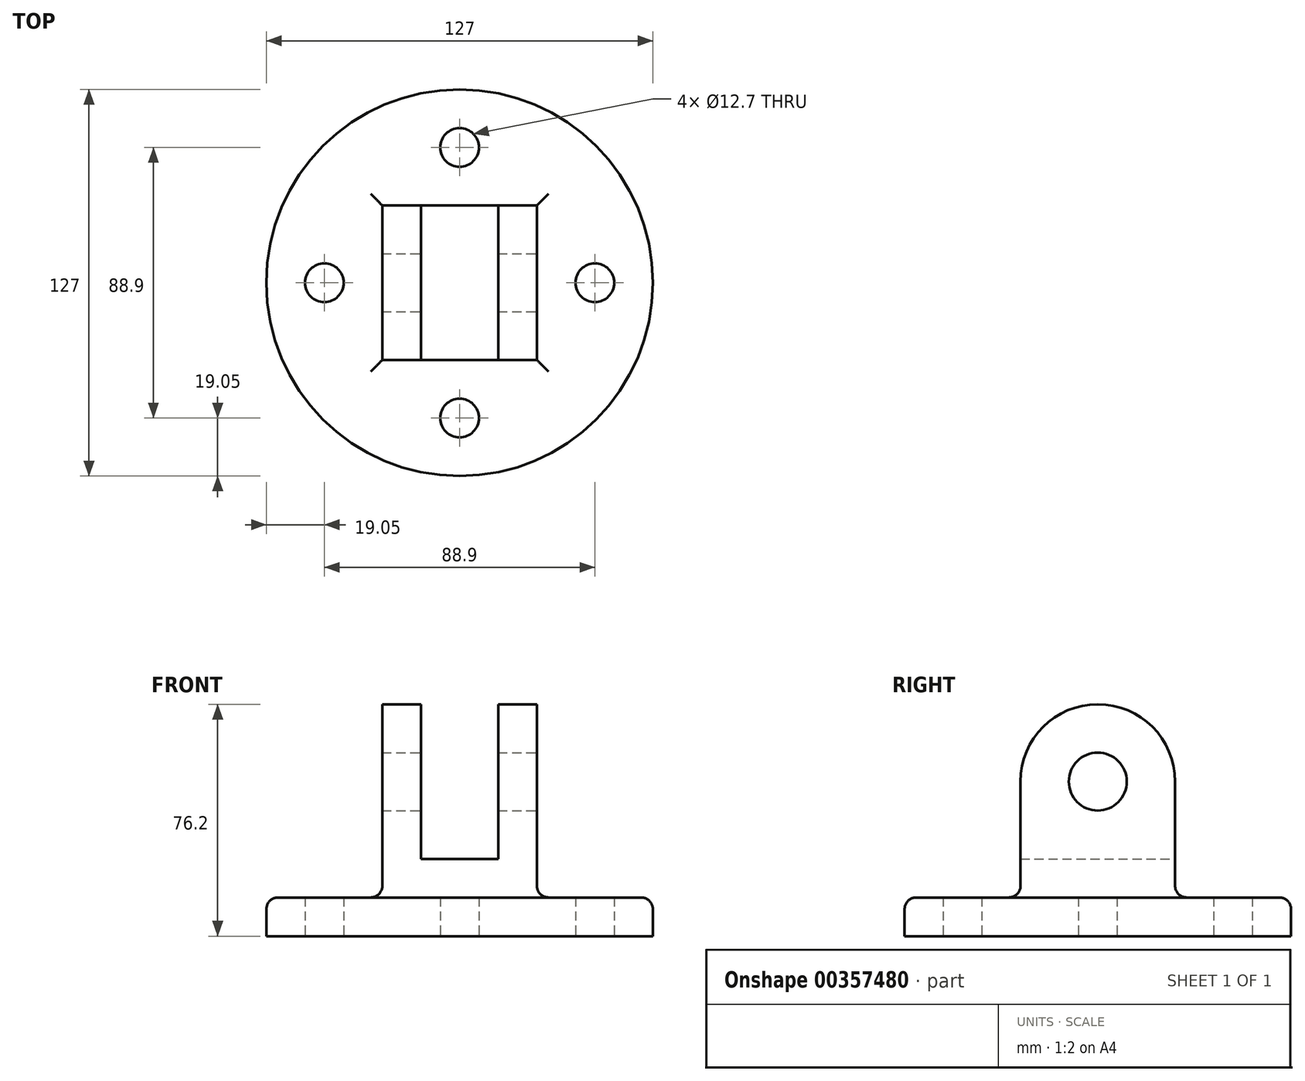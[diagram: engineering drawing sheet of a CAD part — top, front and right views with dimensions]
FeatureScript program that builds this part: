
annotation { "Feature Type Name" : "Feature", "Feature Type Description" : "" }
export const myFeature = defineFeature(function(context is Context, id is Id, definition is map)
    precondition{}
    {
        {
            var Q0;
            Q0=qCreatedBy(makeId("Top.planeOp"),FACE);
            var sketch = newSketch(context, id + "F0", { "sketchPlane" : qUnion([Q0])});
            skCircle(sketch, "E0", {"center": v(0, 0) * mm, "radius": 63.5 * mm});
            skCircle(sketch, "E1", {"center": v(0, 0) * mm, "radius": 44.45 * mm, "construction": true});
            skCircle(sketch, "E2", {"center": v(0, 44.45) * mm, "radius": 6.35 * mm});
            skCircle(sketch, "E3", {"center": v(-44.45, 0) * mm, "radius": 6.35 * mm});
            skCircle(sketch, "E4", {"center": v(44.45, 0) * mm, "radius": 6.35 * mm});
            skCircle(sketch, "E5", {"center": v(0, -44.45) * mm, "radius": 6.35 * mm});
            skSolve(sketch);
        }
        {
            var Q0;
            Q0 = qSketchRegion(id + "F0", true);
            extrude(context, id + "F1", {"entities" : qUnion([Q0]), "depth" : 12.7 * mm});
        }
        {
            var Q0;
            Q0=qCreatedBy(makeId("Front.planeOp"),FACE);
            var sketch = newSketch(context, id + "F2", { "sketchPlane" : qUnion([Q0])});
            skLineSegment(sketch, "E6", {"start": v(-25.4, 0) * mm, "end": v(25.4, 0) * mm});
            skLineSegment(sketch, "E7", {"start": v(-25.4, 0) * mm, "end": v(-25.4, 76.2) * mm});
            skLineSegment(sketch, "E8", {"start": v(25.4, 76.2) * mm, "end": v(25.4, 0) * mm});
            skLineSegment(sketch, "E9", {"start": v(-25.4, 76.2) * mm, "end": v(-12.7, 76.2) * mm});
            skLineSegment(sketch, "E10", {"start": v(-12.7, 76.2) * mm, "end": v(-12.7, 25.4) * mm});
            skLineSegment(sketch, "E11", {"start": v(-12.7, 25.4) * mm, "end": v(12.7, 25.4) * mm});
            skLineSegment(sketch, "E12", {"start": v(12.7, 25.4) * mm, "end": v(12.7, 76.2) * mm});
            skLineSegment(sketch, "E13", {"start": v(12.7, 76.2) * mm, "end": v(25.4, 76.2) * mm});
            skLineSegment(sketch, "E14", {"start": v(0, 70.93) * mm, "end": v(0, -31.27) * mm});
            skSolve(sketch);
        }
        {
            var Q0;
            Q0 = qSketchRegion(id + "F2", true);
            extrude(context, id + "F3", {"entities" : qUnion([Q0]), "operationType" : NewBodyOperationType.ADD, "depth" : 25.4 * mm, "hasSecondDirection" : true, "secondDirectionOppositeDirection" : true, "secondDirectionDepth" : 25.4 * mm});
        }
        {
            var Q0;
            Q0=makeQuery(id+"F3.opExtrude","SWEPT_FACE",FACE,{"disambiguationData":[OSD([sQuery(id+"F2.wireOp",EDGE,"E8")])]});
            var sketch = newSketch(context, id + "F4", { "sketchPlane" : qUnion([Q0])});
            skLineSegment(sketch, "E15", {"start": v(-25.4, 12.7) * mm, "end": v(25.4, 12.7) * mm});
            skLineSegment(sketch, "E16", {"start": v(-25.4, 12.7) * mm, "end": v(-25.4, 50.8) * mm});
            skLineSegment(sketch, "E17", {"start": v(25.4, 12.7) * mm, "end": v(25.4, 50.8) * mm});
            skArc(sketch, "E18", {"start": v(25.4, 50.8) * mm, "mid": v(0, 76.2) * mm, "end": v(-25.4, 50.8) * mm});
            skCircle(sketch, "E19", {"center": v(0, 50.8) * mm, "radius": 9.53 * mm});
            skSolve(sketch);
        }
        {
            var Q0;
            Q0=makeQuery(id+"F4.imprint","IMPRINT",FACE,{"disambiguationData":[TD([[makeQuery(id+"F4.imprint","IMPRINT",EDGE,{"derivedFrom":sQuery(id+"F4.wireOp",EDGE,"E19")}),1.0]])]});
            var Q1;
            {var subQ0=sQuery(id+"F4.wireOp",EDGE,"E18");var subQ1=sQuery(id+"F2.wireOp",EDGE,"E8");var subQ2=makeQuery(id+"F3.opExtrude","CAP_EDGE",EDGE,{"disambiguationData":[OSD([subQ1])],"isStart":true});var subQ3=makeQuery(id+"F4.imprint","INTERSECT",VERTEX,{"derivedFrom":[subQ2,sQuery(id+"F4.wireOp",EDGE,"E17"),subQ0]});Q1=makeQuery(id+"F4.imprint","IMPRINT",FACE,{"disambiguationData":[TD([[makeQuery(id+"F4.imprint","IMPRINT",EDGE,{"disambiguationData":[TD([[subQ3,-1.0]])],"derivedFrom":subQ0}),-1.0]])]});}
            var Q2;
            {var subQ0=sQuery(id+"F4.wireOp",EDGE,"E18");var subQ1=sQuery(id+"F2.wireOp",EDGE,"E8");var subQ2=makeQuery(id+"F3.opExtrude","CAP_EDGE",EDGE,{"disambiguationData":[OSD([subQ1])],"isStart":false});var subQ3=makeQuery(id+"F4.imprint","INTERSECT",VERTEX,{"derivedFrom":[subQ2,sQuery(id+"F4.wireOp",EDGE,"E16"),subQ0]});Q2=makeQuery(id+"F4.imprint","IMPRINT",FACE,{"disambiguationData":[TD([[makeQuery(id+"F4.imprint","IMPRINT",EDGE,{"disambiguationData":[TD([[subQ3,1.0]])],"derivedFrom":subQ0}),-1.0]])]});}
            extrude(context, id + "F5", {"entities" : qUnion([Q0, Q1, Q2]), "operationType" : NewBodyOperationType.REMOVE, "endBound" : BoundingType.THROUGH_ALL, "oppositeDirection" : true, "depth" : 25.4 * mm});
        }
        {
            var Q0;
            Q0=makeQuery(id+"F1.opExtrude","CAP_EDGE",EDGE,{"disambiguationData":[OSD([sQuery(id+"F0.wireOp",EDGE,"E0")])],"isStart":false});
            fillet(context, id + "F6", {"entities" : qUnion([Q0]), "radius" : 3.8 * mm, "tangentPropagation" : true, "allowEdgeOverflow" : false});
        }
        {
            var Q0;
            Q0=makeQuery(id+"F3.boolean.opBoolean","INTERSECT",EDGE,{"derivedFrom":[makeQuery(id+"F1.opExtrude","CAP_FACE",FACE,{"disambiguationData":[OSD([sQuery(id+"F0.wireOp",EDGE,"E0"),sQuery(id+"F0.wireOp",EDGE,"E2"),sQuery(id+"F0.wireOp",EDGE,"E3"),sQuery(id+"F0.wireOp",EDGE,"E4"),sQuery(id+"F0.wireOp",EDGE,"E5")])],"isStart":false}),makeQuery(id+"F3.opExtrude","CAP_FACE",FACE,{"disambiguationData":[OSD([sQuery(id+"F2.wireOp",EDGE,"E6"),sQuery(id+"F2.wireOp",EDGE,"E7"),sQuery(id+"F2.wireOp",EDGE,"E8"),sQuery(id+"F2.wireOp",EDGE,"E9"),sQuery(id+"F2.wireOp",EDGE,"E10"),sQuery(id+"F2.wireOp",EDGE,"E11"),sQuery(id+"F2.wireOp",EDGE,"E12"),sQuery(id+"F2.wireOp",EDGE,"E13")])],"isStart":false})]});
            var Q1;
            Q1=makeQuery(id+"F3.boolean.opBoolean","INTERSECT",EDGE,{"derivedFrom":[makeQuery(id+"F1.opExtrude","CAP_FACE",FACE,{"disambiguationData":[OSD([sQuery(id+"F0.wireOp",EDGE,"E0"),sQuery(id+"F0.wireOp",EDGE,"E2"),sQuery(id+"F0.wireOp",EDGE,"E3"),sQuery(id+"F0.wireOp",EDGE,"E4"),sQuery(id+"F0.wireOp",EDGE,"E5")])],"isStart":false}),makeQuery(id+"F3.opExtrude","SWEPT_FACE",FACE,{"disambiguationData":[OSD([sQuery(id+"F2.wireOp",EDGE,"E8")])]})]});
            var Q2;
            Q2=makeQuery(id+"F3.boolean.opBoolean","INTERSECT",EDGE,{"derivedFrom":[makeQuery(id+"F1.opExtrude","CAP_FACE",FACE,{"disambiguationData":[OSD([sQuery(id+"F0.wireOp",EDGE,"E0"),sQuery(id+"F0.wireOp",EDGE,"E2"),sQuery(id+"F0.wireOp",EDGE,"E3"),sQuery(id+"F0.wireOp",EDGE,"E4"),sQuery(id+"F0.wireOp",EDGE,"E5")])],"isStart":false}),makeQuery(id+"F3.opExtrude","CAP_FACE",FACE,{"disambiguationData":[OSD([sQuery(id+"F2.wireOp",EDGE,"E6"),sQuery(id+"F2.wireOp",EDGE,"E7"),sQuery(id+"F2.wireOp",EDGE,"E8"),sQuery(id+"F2.wireOp",EDGE,"E9"),sQuery(id+"F2.wireOp",EDGE,"E10"),sQuery(id+"F2.wireOp",EDGE,"E11"),sQuery(id+"F2.wireOp",EDGE,"E12"),sQuery(id+"F2.wireOp",EDGE,"E13")])],"isStart":true})]});
            var Q3;
            Q3=makeQuery(id+"F3.boolean.opBoolean","INTERSECT",EDGE,{"derivedFrom":[makeQuery(id+"F1.opExtrude","CAP_FACE",FACE,{"disambiguationData":[OSD([sQuery(id+"F0.wireOp",EDGE,"E0"),sQuery(id+"F0.wireOp",EDGE,"E2"),sQuery(id+"F0.wireOp",EDGE,"E3"),sQuery(id+"F0.wireOp",EDGE,"E4"),sQuery(id+"F0.wireOp",EDGE,"E5")])],"isStart":false}),makeQuery(id+"F3.opExtrude","SWEPT_FACE",FACE,{"disambiguationData":[OSD([sQuery(id+"F2.wireOp",EDGE,"E7")])]})]});
            fillet(context, id + "F7", {"entities" : qUnion([Q0, Q1, Q2, Q3]), "radius" : 3.8 * mm, "tangentPropagation" : true, "allowEdgeOverflow" : false});
        }
    });
